SOLIDWORKS PART (.sldprt)
format: sldprt  version: not decoded by parser v0  size: 120,832 bytes
history: native  units: mm
features: sketch x7, cut_extrude x5, extrude x2, fillet x1 + 4 further entries (+9 scaffold rows collapsed; 6 parser-record rows omitted)
feature tree (34):
  scaffold x9  (default folders/planes/origin — collapsed)
  parser-record x6  (decoder bookkeeping rows leaked as tree rows — omitted from the tree; the rows remain in map.json)
  "ID2"
  "ID3"
  sketch  "Sketch1"  dims[D1=76.2mm D2=44.7802mm]
  extrude  "Base-Extrude"  Depth=6.35mm
  sketch  "Sketch2"  dims[D2=12.7mm D1=38.1mm D3=13.462mm]
  cut_extrude  "Cut-Extrude1"  [1 undecoded]
  sketch  "Sketch4"  dims[D1=12.7mm D2=38.1mm D3=38.1mm]
  cut_extrude  "Cut-Extrude2"  [1 undecoded]
  sketch  "Sketch5"  dims[D1=12.7mm D2=~37.934697mm]
  cut_extrude  "Cut-Extrude3"  [1 undecoded]
  sketch  "Sketch6"  dims[D1=6.223mm D2=6.0198mm D3=15.875mm]
  extrude  "Boss-Extrude1"  [1 undecoded]
  sketch  "Sketch7"  dims[c1.D1=~6.421564mm c2.D1=45.0deg]
  cut_extrude  "Cut-Extrude4"  Depth=75.817006mm
  sketch  "Sketch8"  dims[c1.D1=~5.046732mm c2.D1=45.0deg]
  cut_extrude  "Cut-Extrude5"  Depth=75.817006mm
  fillet  "Fillet2"  Radius=1.27mm
  "ID4"
  "ID5"
decode coverage: 11 of 15 modeling features carry decoded parameters; 4 rows unclassified (native names shown)
note: ~ marks probable driven/reference dimensions
note: 4 parameter values undecoded
summary: no parameter record found for 4 features
note: suppression state not decoded; provenance and decode notes live in map.json
